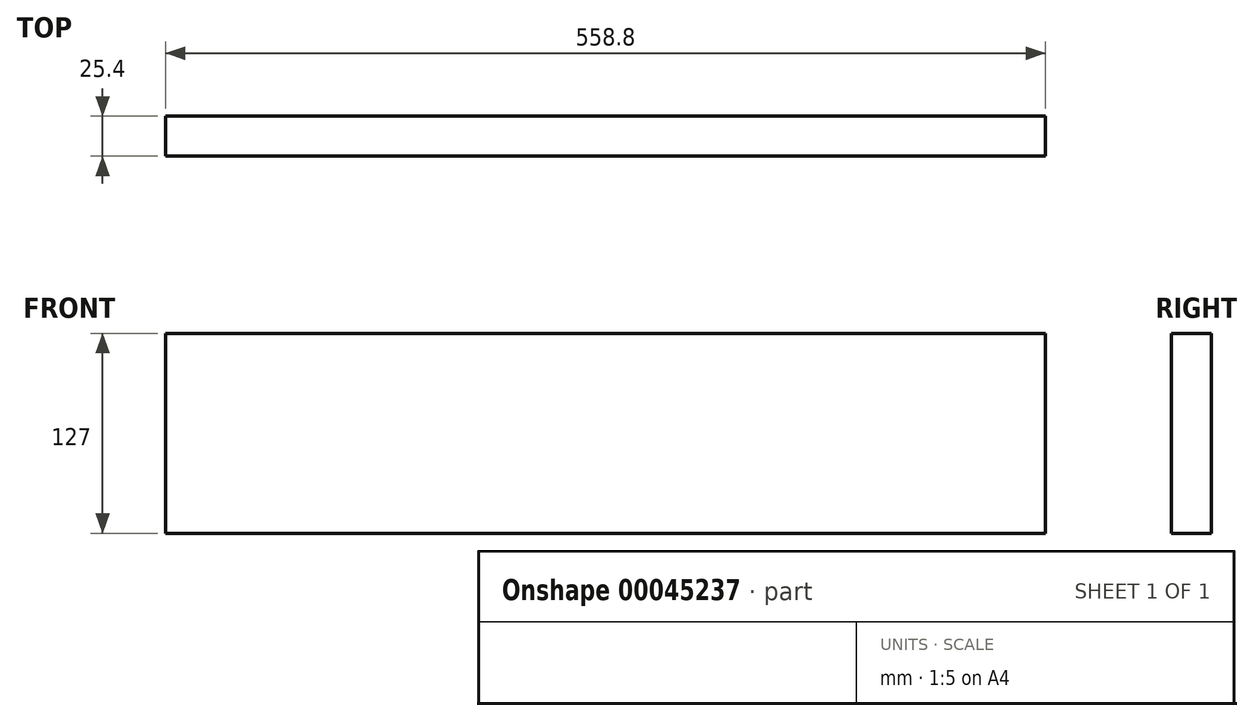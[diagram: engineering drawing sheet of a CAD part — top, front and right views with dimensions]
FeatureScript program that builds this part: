
annotation { "Feature Type Name" : "Feature", "Feature Type Description" : "" }
export const myFeature = defineFeature(function(context is Context, id is Id, definition is map)
    precondition{}
    {
        {
            var Q0;
            Q0=qCreatedBy(makeId("Front.planeOp"),FACE);
            var sketch = newSketch(context, id + "F0", { "sketchPlane" : qUnion([Q0])});
            skLineSegment(sketch, "E0.rect.bottom", {"start": v(279.4, -63.5) * mm, "end": v(-279.4, -63.5) * mm});
            skLineSegment(sketch, "E0.rect.top", {"start": v(279.4, 63.5) * mm, "end": v(-279.4, 63.5) * mm});
            skLineSegment(sketch, "E0.rect.left", {"start": v(279.4, -63.5) * mm, "end": v(279.4, 63.5) * mm});
            skLineSegment(sketch, "E0.rect.right", {"start": v(-279.4, -63.5) * mm, "end": v(-279.4, 63.5) * mm});
            skPoint(sketch, "E0.rect.middle", {"position": v(0, 0) * mm});
            skSolve(sketch);
        }
        {
            var Q0;
            Q0=makeQuery(id+"F0.imprint","IMPRINT",FACE,{"disambiguationData":[TD([[makeQuery(id+"F0.imprint","IMPRINT",EDGE,{"derivedFrom":sQuery(id+"F0.wireOp",EDGE,"E0.rect.bottom")}),-1.0]])]});
            extrude(context, id + "F1", {"entities" : qUnion([Q0]), "depth" : 25.4 * mm});
        }
    });
